# Revit family: IS_iLifeA_T4675_BIM_NL
name_source: partatom
category: Plumbing Fixtures
units: mm (PartAtom-declared; Revit-internal decimal feet)

## family parameters
Always vertical = No
Cut with Voids When Loaded = No
OmniClass Number = 23.45.05.21.11.11
OmniClass Title = Water Operated Water Closets
Part Type = Normal
Room Calculation Point = No
Round Connector Dimension = Use Diameter
Shared = No
Work Plane-Based = No

## types (1)
- T467501 - I.life A sandwich seat universal shape - White
    Accesoires = https://www.idealstandard.nl
    Accessories = https://www.idealstandard.nl
    Afmetingen = 455 x 48 x 367mm
    AfstandsEenheid = millimeter
    Afwerking = Weiß
    AreaMeasurement = internal
    AreaUnits = Millimeter
    Artikelnummer = T467501
    Artikelomschrijving = I.life A Sandwich-Sitz Universalform - Weiß
    Artikelreferentie = I.life Ein Sandwich-Sitz Universalform
    Auteur = Ideal Standard
    BIMObjectName = IS_IdealStandard_WCseatsandcovers__I.life__T4675
    BIMobject category = Toilet Seats
    BIMobject category code = sanitary-toilet-seats
    BIMobject main category = Sanitary
    BIMobject main category code = sanitary
    BarCode = 8014140486084
    Barcode = 8014140486084
    Beschrijvinggarantie = Herstellergarantie
    BimObjectNaam = IS_IdealStandard_WCseatsandcovers__I.life__T4675
    Brand = Ideal Standard
    Brand url = http://https:
    Breedte = 0
    BrutoGewicht = 0
    Color = Weiß
    ConnectionType = Plumbing
    Cost = 0 $
    CurrencyUnit = €
    CurrentRevision = 1
    Date of publishing = 28/06/2021
    Description = I.life A Sandwich-Sitz Universalform - Weiß
    Diepte = 0 mm  [stored 0 ft]
    DrainSize = 0 mm  [stored 0 ft]
    DurationUnit = Years
    DuurEenheid = Jaar
    Edition number = 1
    Eigenschappen = Sandwichsitz Universalform universal
    Features = sandwich seat universal shape
    Finish = Weiß
    GTIN code = https://8014140486084
    Garantieonderdelen = 5
    Garantieunits = Jaar
    GemaaktOp = 40722
    GrootteAfvoergat = 0
    Help = https://www.idealstandard.nl
    Hoogte = 48.0092148780823
    Hulp = https://www.idealstandard.nl
    IFC Classification = Sanitary Terminal
    IfcExportAs = IfcSanitaryTerminalType
    IfcExportType = WCSEAT
    Installatieinstructies = https://www.idealstandard.nl
    Installation instructions = https://www.idealstandard.nl
    InstallationInstructions = https://www.idealstandard.nl
    Kleur = Weiß
    Kleurwc = Weiß
    Lengte = 455 mm
    LinearUnits = millimeter
    MainColor = White
    MaintenanceInformation = https://www.idealstandard.nl
    Manufacturer = Ideal Standard
    Manufacturer name = Ideal Standard
    ManufacturerURL = https://www.idealstandard.nl
    Materiaal = urea
    MateriaalWC = urea
    Material = urea
    Material main = urea
    Merk = Ideal Standard
    Model = T467501
    ModelNumber = T467501
    ModelReference = I.life A sandwich seat universal shape
    Montageinstuctie = https://www.idealstandard.nl
    NBS Reference Code = 45-35-70/391
    NBS Reference Description = WC seats and covers
    Name = WCseatsandcovers__I.life__T4675_IdealStandard
    NettWeight = 2.2
    Nettogewicht = 2.2
    NominalDepth = 455 mm
    NominalHeight = 48 mm
    NominalWidth = 367 mm
    Normen = WCseatsandcovers__I.life__T4675_IdealStandard
    OppervlakteEenheid = Millimeter
    Overloop = 0 mm  [stored 0 ft]
    PanColor = White
    PanMaterial = urea
    Product Guid = 546575aa-a366-4722-b858-2d0636095b87
    Product SKU = T4675
    Product certification = https://www.idealstandard.nl
    Product data url = https://bimobject.com
    Product family = I.life
    Product group = Toilet seat
    Product name = I.life A sandwich seat universal shape
    Product url = https://www.idealstandard.nl
    ProductInformation = https://www.idealstandard.nl
    ProductSoort = WC-Sitze
    Productinformatie = https://www.idealstandard.nl
    QR code = http://bimobject.com
    Referentie = I.life Ein Sandwich-Sitz Universalform
    Revisie = 1
    Shape = sculpture
    Size = 455 x 48 x 367mm
    Space = Internal
    SpareParts = https://www.idealstandard.nl
    Technical description = https://www.idealstandard.nl
    Telefoonnummer = 077 355 08 08
    Typeconnectie = Installation
    URL = https://https:
    Uniclass2015Beschrijving = WC seats and covers
    Uniclass2015Code = Pr_40_20_93_95
    Uniclass2015Referentie = Pr_40_20_93_95
    Uniclass2015Title = WC seats and covers
    Uniclass2015Version = v1.20
    Urlproducent = https://https:
    ValutaEenheid = €
    Versie = 1
    Version = 1
    Vervangingskosten = 0
    VolumeUnits = Liter
    Volumeunits = Liter
    Vorm = beeldhouwwerk
    WRASURL = https://www.wrasapprovals.co.uk
    WarrantyDescription = manufacturer warranty
    WarrantyDurationParts = 99
    WarrantyDurationUnit = years
    Wisselstukken = https://www.idealstandard.nl
    Youtube clip = https://www.youtube.com

note: [stored X ft] marks values corroborated as IEEE doubles in the binary element streams (Revit-internal decimal feet)

## geometry (parser evidence)
native form markers: Sweep x3
no freeform markers — native parametric forms only
